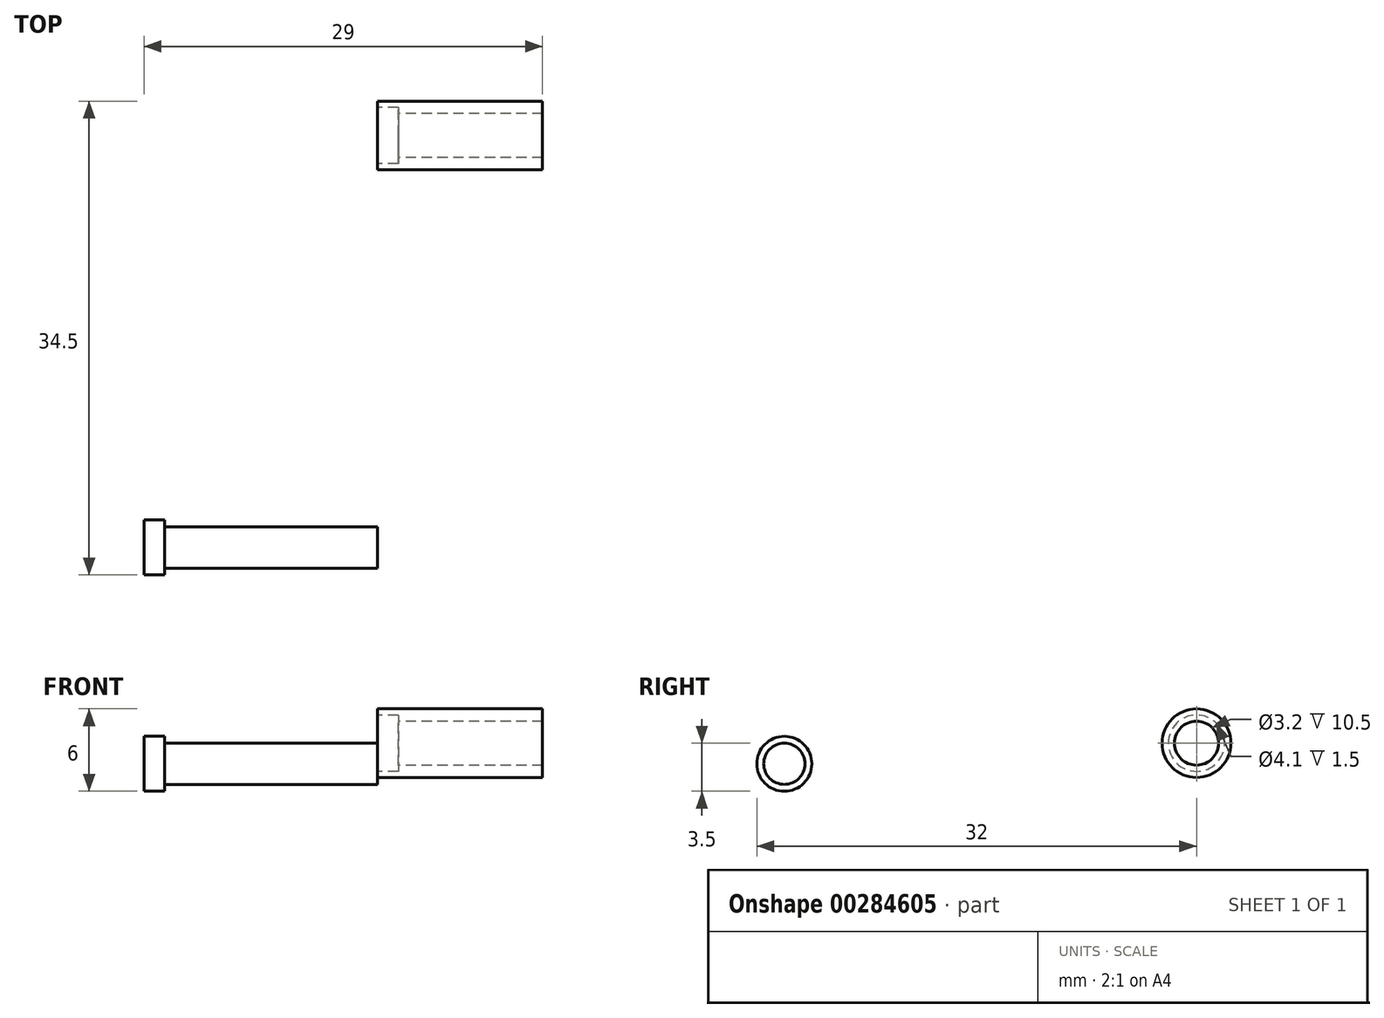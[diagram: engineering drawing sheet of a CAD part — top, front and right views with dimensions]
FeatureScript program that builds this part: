
annotation { "Feature Type Name" : "Feature", "Feature Type Description" : "" }
export const myFeature = defineFeature(function(context is Context, id is Id, definition is map)
    precondition{}
    {
        {
            var Q0;
            Q0=qCreatedBy(makeId("Front.planeOp"),FACE);
            var sketch = newSketch(context, id + "F0", { "sketchPlane" : qUnion([Q0])});
            skLineSegment(sketch, "E0", {"start": v(0, 0) * mm, "end": v(-15.5, 0) * mm});
            skLineSegment(sketch, "E1", {"start": v(-15.5, 0) * mm, "end": v(-15.5, 0.5) * mm});
            skLineSegment(sketch, "E2", {"start": v(-15.5, 0.5) * mm, "end": v(-17, 0.5) * mm});
            skLineSegment(sketch, "E3", {"start": v(-17, 0.5) * mm, "end": v(-17, -1.5) * mm});
            skLineSegment(sketch, "E4", {"start": v(-17, -1.5) * mm, "end": v(0, -1.5) * mm});
            skLineSegment(sketch, "E5", {"start": v(0, -1.5) * mm, "end": v(0, 0) * mm});
            skSolve(sketch);
        }
        {
            var Q0;
            Q0=qCreatedBy(makeId("Right.planeOp"),FACE);
            var sketch = newSketch(context, id + "F1", { "sketchPlane" : qUnion([Q0])});
            skLineSegment(sketch, "E6", {"start": v(0, 0) * mm, "end": v(30, 0) * mm, "construction": true});
            skCircle(sketch, "E7", {"center": v(30, 0) * mm, "radius": 2.5 * mm});
            skCircle(sketch, "E8", {"center": v(30, 0) * mm, "radius": 1.6 * mm});
            skSolve(sketch);
        }
        {
            var Q0;
            Q0=makeQuery(id+"F1.imprint","IMPRINT",FACE,{"disambiguationData":[TD([[makeQuery(id+"F1.imprint","IMPRINT",EDGE,{"derivedFrom":sQuery(id+"F1.wireOp",EDGE,"E7")}),1.0]])]});
            extrude(context, id + "F2", {"entities" : qUnion([Q0]), "depth" : 12 * mm});
        }
        {
            var Q0;
            Q0=makeQuery(id+"F0.imprint","IMPRINT",FACE,{"disambiguationData":[TD([[makeQuery(id+"F0.imprint","IMPRINT",EDGE,{"derivedFrom":sQuery(id+"F0.wireOp",EDGE,"E0")}),1.0]])]});
            var Q1;
            Q1=sQuery(id+"F0.wireOp",EDGE,"E4");
            revolve(context, id + "F3", {"entities" : qUnion([Q0]), "axis" : qUnion([Q1]), "revolveType" : RevolveType.FULL});
        }
        {
            var Q0;
            Q0=makeQuery(id+"F2.opExtrude","CAP_FACE",FACE,{"disambiguationData":[OSD([sQuery(id+"F1.wireOp",EDGE,"E7"),sQuery(id+"F1.wireOp",EDGE,"E8")])],"isStart":true});
            var sketch = newSketch(context, id + "F4", { "sketchPlane" : qUnion([Q0])});
            skCircle(sketch, "E9.0", {"center": v(-30, 0) * mm, "radius": 1.6 * mm});
            skCircle(sketch, "E10", {"center": v(-30, 0) * mm, "radius": 2.05 * mm});
            skSolve(sketch);
        }
        {
            var Q0;
            Q0=makeQuery(id+"F4.imprint","IMPRINT",FACE,{"disambiguationData":[TD([[makeQuery(id+"F4.imprint","IMPRINT",EDGE,{"derivedFrom":sQuery(id+"F4.wireOp",EDGE,"E9.0")}),1.0]])]});
            extrude(context, id + "F5", {"entities" : qUnion([Q0]), "operationType" : NewBodyOperationType.REMOVE, "oppositeDirection" : true, "depth" : 1.5 * mm});
        }
    });
